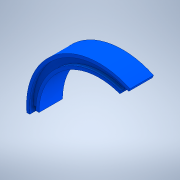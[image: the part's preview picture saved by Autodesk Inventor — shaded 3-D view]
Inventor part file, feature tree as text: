
AUTODESK INVENTOR PART (.ipt)
format: ipt  version: 2020 (Build 240168000, 168)  size: 139,264 bytes
history: native  units: mm
features: revolve x2, sketch x1
ambient origin geometry x8: Origin, YZ Plane, XZ Plane, XY Plane, X Axis, Y Axis, Z Axis, Center Point
bodies: Solid1 (feature_tree)
feature tree (3):
  sketch  "Sketch1"  dims[d0=1.0mm d1=7.5mm d2=2.0mm d3=1.0mm d4=1.1mm d5=1.1mm d6=20.2mm d7=19.198622mm d8=0.872665mm d9=20.071286mm]
  revolve  "Revolution1"  [1 undecoded]
  revolve  "Revolution2"  [1 undecoded]
note: 2 required parameter values undecoded (feature->parameter linkage not recoverable at this tier; creation-order binding heuristic only, values carry confidence <= 0.55)
